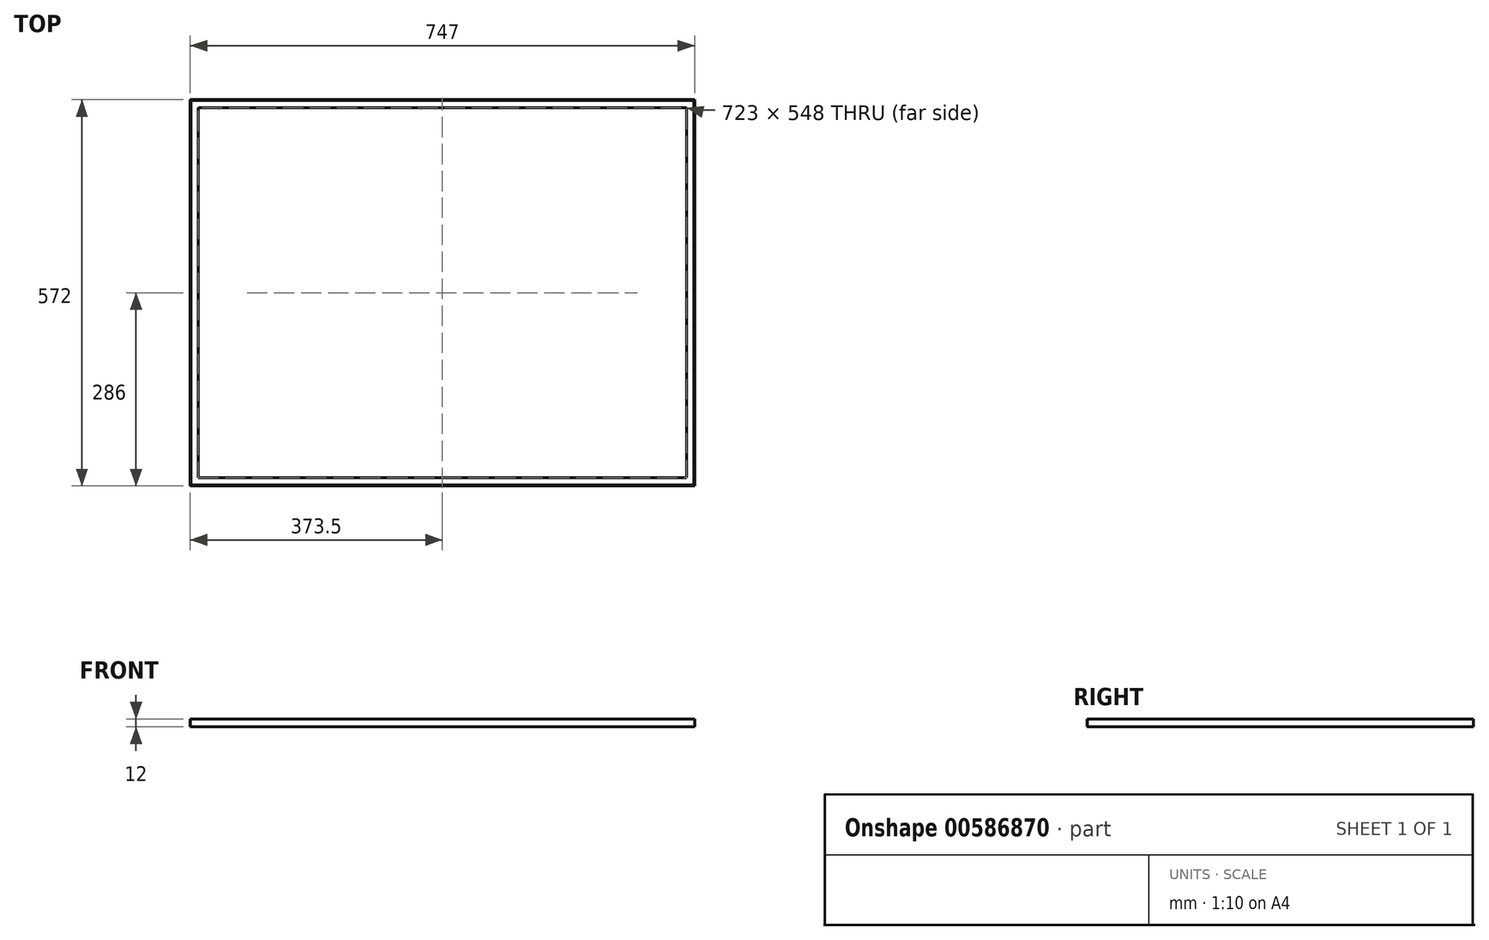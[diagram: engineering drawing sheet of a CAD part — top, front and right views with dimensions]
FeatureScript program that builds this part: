
annotation { "Feature Type Name" : "Feature", "Feature Type Description" : "" }
export const myFeature = defineFeature(function(context is Context, id is Id, definition is map)
    precondition{}
    {
        {
            var Q0;
            Q0=qCreatedBy(makeId("Top.planeOp"),FACE);
            var sketch = newSketch(context, id + "F0", { "sketchPlane" : qUnion([Q0])});
            skLineSegment(sketch, "E0.bottom", {"start": v(373.5, 286) * mm, "end": v(-373.5, 286) * mm});
            skLineSegment(sketch, "E0.top", {"start": v(373.5, -286) * mm, "end": v(-373.5, -286) * mm});
            skLineSegment(sketch, "E0.left", {"start": v(373.5, 286) * mm, "end": v(373.5, -286) * mm});
            skLineSegment(sketch, "E0.right", {"start": v(-373.5, 286) * mm, "end": v(-373.5, -286) * mm});
            skPoint(sketch, "E0.middle", {"position": v(0, 0) * mm});
            skSolve(sketch);
        }
        {
            var Q0;
            Q0=qCreatedBy(makeId("Front.planeOp"),FACE);
            var sketch = newSketch(context, id + "F1", { "sketchPlane" : qUnion([Q0])});
            skLineSegment(sketch, "E1", {"start": v(-373.5, 12) * mm, "end": v(-373.5, 0) * mm});
            skLineSegment(sketch, "E2", {"start": v(-373.5, 0) * mm, "end": v(-361.5, 0) * mm});
            skLineSegment(sketch, "E3.0", {"start": v(-372.3, 1.2) * mm, "end": v(-361.5, 1.2) * mm});
            skLineSegment(sketch, "E3.1", {"start": v(-372.3, 12) * mm, "end": v(-372.3, 1.2) * mm});
            skLineSegment(sketch, "E4", {"start": v(-373.5, 12) * mm, "end": v(-372.3, 12) * mm});
            skLineSegment(sketch, "E5", {"start": v(-361.5, 1.2) * mm, "end": v(-361.5, 0) * mm});
            skSolve(sketch);
        }
        {
            var Q0;
            Q0=makeQuery(id+"F1.imprint","IMPRINT",FACE,{"disambiguationData":[TD([[makeQuery(id+"F1.imprint","IMPRINT",EDGE,{"derivedFrom":sQuery(id+"F1.wireOp",EDGE,"E1")}),1.0]])]});
            var Q1;
            Q1=sQuery(id+"F0.wireOp",EDGE,"E0.right");
            var Q2;
            Q2=sQuery(id+"F0.wireOp",EDGE,"E0.top");
            var Q3;
            Q3=sQuery(id+"F0.wireOp",EDGE,"E0.left");
            var Q4;
            Q4=sQuery(id+"F0.wireOp",EDGE,"E0.bottom");
            sweep(context, id + "F2", {"profiles" : qUnion([Q0]), "path" : qUnion([Q1, Q2, Q3, Q4])});
        }
    });
